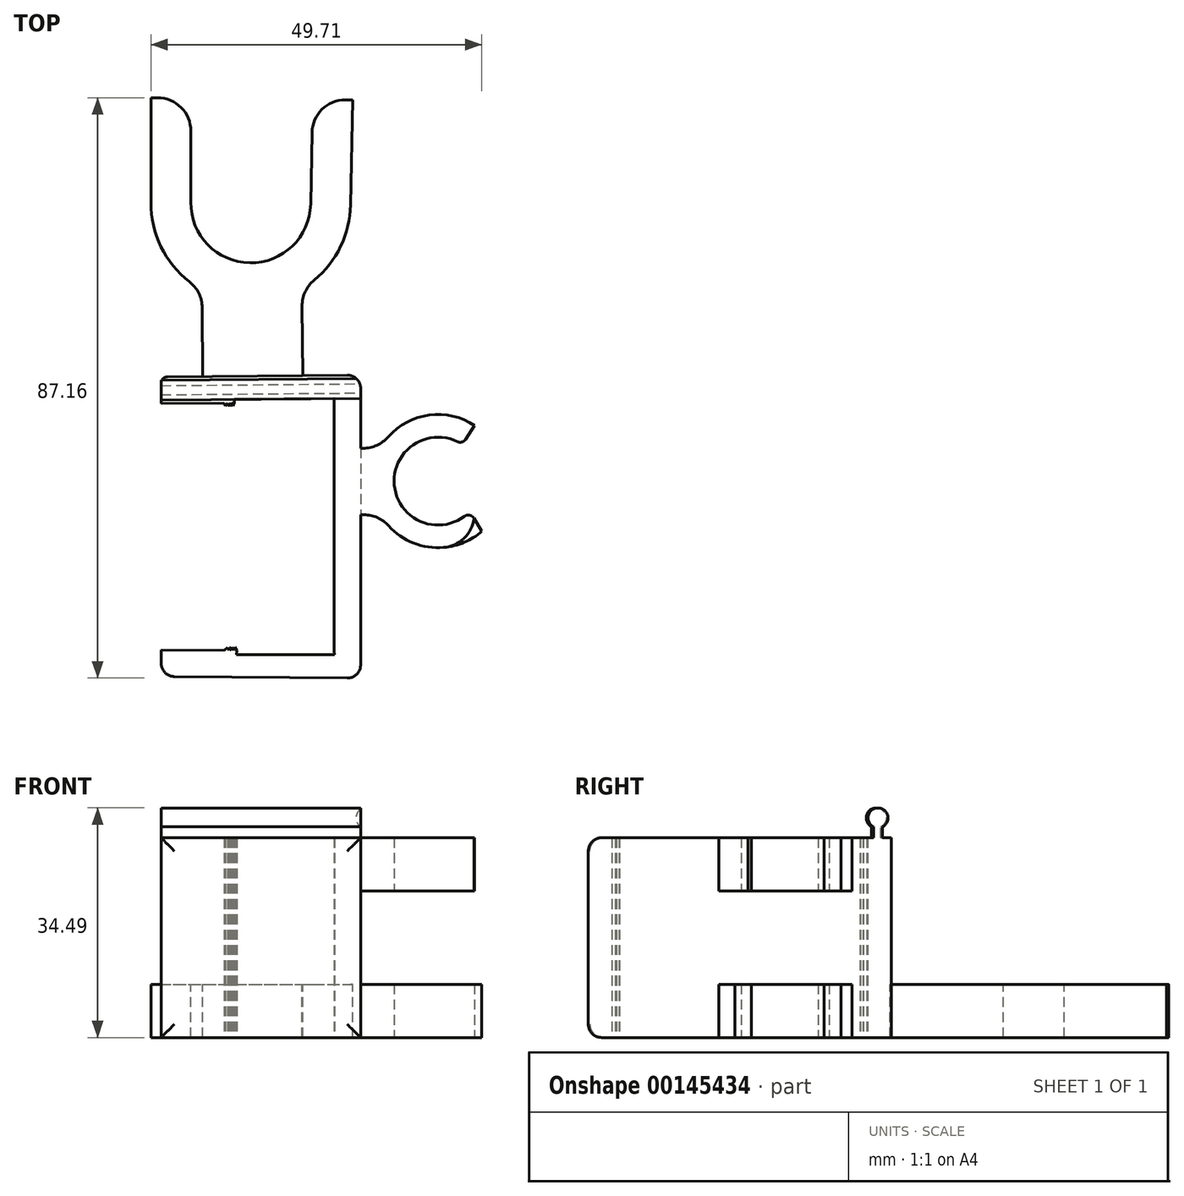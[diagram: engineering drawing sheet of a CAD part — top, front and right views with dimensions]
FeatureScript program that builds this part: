
annotation { "Feature Type Name" : "Feature", "Feature Type Description" : "" }
export const myFeature = defineFeature(function(context is Context, id is Id, definition is map)
    precondition{}
    {
        {
            var Q0;
            Q0=qCreatedBy(makeId("Top.planeOp"),FACE);
            var sketch = newSketch(context, id + "F0", { "sketchPlane" : qUnion([Q0])});
            skLineSegment(sketch, "E0", {"start": v(-19.4, 17.85) * mm, "end": v(-9.96, 17.94) * mm});
            skLineSegment(sketch, "E1", {"start": v(6.6, 18.08) * mm, "end": v(6.6, -19.37) * mm});
            skLineSegment(sketch, "E2", {"start": v(-19.4, 17.85) * mm, "end": v(-19.43, 21.85) * mm});
            skLineSegment(sketch, "E3", {"start": v(-19.43, 21.85) * mm, "end": v(10.57, 22.12) * mm});
            skLineSegment(sketch, "E4", {"start": v(10.57, 22.12) * mm, "end": v(10.57, -23.4) * mm});
            skLineSegment(sketch, "E5", {"start": v(-19.4, -19.15) * mm, "end": v(-19.4, -23.15) * mm});
            skLineSegment(sketch, "E6", {"start": v(-19.4, -23.15) * mm, "end": v(10.57, -23.4) * mm});
            skPoint(sketch, "E7", {"position": v(-8.4, 17.95) * mm});
            skLineSegment(sketch, "E8", {"start": v(6.6, -0.65) * mm, "end": v(-3.27, -0.73) * mm, "construction": true});
            skPoint(sketch, "E9.MirrorP", {"position": v(-8.06, -19.5) * mm});
            skLineSegment(sketch, "E10.MirrorCS", {"start": v(-8.6, 17.45) * mm, "end": v(-8.92, 17.94) * mm});
            skLineSegment(sketch, "E11.MirrorCS", {"start": v(-8.92, 17.94) * mm, "end": v(-9.18, 17.43) * mm});
            skLineSegment(sketch, "E12.MirrorCS", {"start": v(-9.75, 17.45) * mm, "end": v(-9.96, 17.94) * mm});
            skLineSegment(sketch, "E13.MirrorCS", {"start": v(-9.44, 17.94) * mm, "end": v(-9.75, 17.45) * mm});
            skLineSegment(sketch, "E14.MirrorCS", {"start": v(-9.18, 17.43) * mm, "end": v(-9.44, 17.94) * mm});
            skLineSegment(sketch, "E15.MirrorCS", {"start": v(-8.4, 17.95) * mm, "end": v(-8.6, 17.45) * mm});
            skPoint(sketch, "E16", {"position": v(-8.02, -19.25) * mm});
            skLineSegment(sketch, "E17", {"start": v(-8.02, -19.25) * mm, "end": v(-8.32, -18.74) * mm});
            skLineSegment(sketch, "E18", {"start": v(-8.32, -18.74) * mm, "end": v(-8.59, -19.24) * mm});
            skLineSegment(sketch, "E19", {"start": v(-8.59, -19.24) * mm, "end": v(-8.83, -18.75) * mm});
            skLineSegment(sketch, "E20", {"start": v(-8.83, -18.75) * mm, "end": v(-9.18, -19.24) * mm});
            skLineSegment(sketch, "E21", {"start": v(-9.18, -19.24) * mm, "end": v(-9.4, -18.76) * mm});
            skLineSegment(sketch, "E22", {"start": v(-9.4, -18.76) * mm, "end": v(-9.9, -19.23) * mm});
            skLineSegment(sketch, "E23.trimOffspring", {"start": v(-9.9, -19.23) * mm, "end": v(-19.4, -19.15) * mm});
            skLineSegment(sketch, "E24.bottom", {"start": v(10.57, 11.13) * mm, "end": v(13.49, 11.13) * mm});
            skLineSegment(sketch, "E24.top", {"start": v(10.57, 1.13) * mm, "end": v(13.56, 1.13) * mm});
            skLineSegment(sketch, "E24.left", {"start": v(10.57, 11.13) * mm, "end": v(10.57, 1.13) * mm});
            skArc(sketch, "E25", {"start": v(25.06, 12.13) * mm, "mid": v(15.61, 5.57) * mm, "end": v(26.12, 0.9) * mm});
            skArc(sketch, "E26", {"start": v(13.56, 1.13) * mm, "mid": v(20.58, -3.68) * mm, "end": v(28.76, -1.34) * mm});
            skPoint(sketch, "E27.orphan", {"position": v(22.18, 11.19) * mm});
            skPoint(sketch, "E28.orphan", {"position": v(22.18, 1.19) * mm});
            skLineSegment(sketch, "E29", {"start": v(26.33, 12.48) * mm, "end": v(27.69, 14.54) * mm});
            skLineSegment(sketch, "E30", {"start": v(27.58, 0.61) * mm, "end": v(28.76, -1.34) * mm});
            skArc(sketch, "E31.trimOffspring", {"start": v(27.69, 14.54) * mm, "mid": v(19.85, 15.91) * mm, "end": v(13.49, 11.13) * mm});
            skPoint(sketch, "E32.visualSharp", {"position": v(25.82, 11.7) * mm});
            skArc(sketch, "E32.filletArc", {"start": v(25.06, 12.13) * mm, "mid": v(25.76, 12.06) * mm, "end": v(26.33, 12.48) * mm});
            skPoint(sketch, "E33.visualSharp", {"position": v(26.96, 1.63) * mm});
            skArc(sketch, "E33.filletArc", {"start": v(27.58, 0.61) * mm, "mid": v(26.91, 1.07) * mm, "end": v(26.12, 0.9) * mm});
            skLineSegment(sketch, "E34", {"start": v(-8.4, 17.95) * mm, "end": v(-8.4, 18.45) * mm});
            skLineSegment(sketch, "E35", {"start": v(-8.4, 18.45) * mm, "end": v(6.6, 18.58) * mm});
            skLineSegment(sketch, "E36", {"start": v(6.6, 18.58) * mm, "end": v(6.6, 18.08) * mm});
            skLineSegment(sketch, "E37", {"start": v(-8.02, -19.25) * mm, "end": v(-8.06, -19.87) * mm});
            skLineSegment(sketch, "E38", {"start": v(-8.06, -19.87) * mm, "end": v(6.63, -19.87) * mm});
            skLineSegment(sketch, "E39", {"start": v(6.63, -19.87) * mm, "end": v(6.6, -19.37) * mm});
            skSolve(sketch);
        }
        {
            var Q0;
            Q0=makeQuery(id+"F0.imprint","IMPRINT",FACE,{"disambiguationData":[TD([[makeQuery(id+"F0.imprint","IMPRINT",EDGE,{"derivedFrom":sQuery(id+"F0.wireOp",EDGE,"E0")}),1.0]])]});
            extrude(context, id + "F1", {"entities" : qUnion([Q0]), "depth" : 30 * mm});
        }
        {
            var Q0;
            Q0=makeQuery(id+"F0.imprint","IMPRINT",FACE,{"disambiguationData":[TD([[makeQuery(id+"F0.imprint","IMPRINT",EDGE,{"derivedFrom":sQuery(id+"F0.wireOp",EDGE,"E24.bottom")}),-1.0]])]});
            extrude(context, id + "F2", {"entities" : qUnion([Q0]), "operationType" : NewBodyOperationType.ADD, "depth" : 8 * mm});
        }
        {
            var Q0;
            Q0=qCreatedBy(makeId("Top.planeOp"),FACE);
            cPlane(context, id + "F3", {"entities" : qUnion([Q0]), "cplaneType" : CPlaneType.OFFSET, "offset" : 22 * mm, "width" : 150 * mm, "height" : 150 * mm});
        }
        {
            var Q0;
            Q0=qCreatedBy(id+"F3.planeOp",FACE);
            var sketch = newSketch(context, id + "F4", { "sketchPlane" : qUnion([Q0])});
            skLineSegment(sketch, "E40.0", {"start": v(-19.4, 17.85) * mm, "end": v(-9.96, 17.94) * mm});
            skLineSegment(sketch, "E40.1", {"start": v(6.6, 18.08) * mm, "end": v(6.6, -19.37) * mm});
            skLineSegment(sketch, "E40.2", {"start": v(6.6, -19.37) * mm, "end": v(-8.02, -19.25) * mm});
            skLineSegment(sketch, "E40.3", {"start": v(-19.4, 17.85) * mm, "end": v(-19.43, 21.85) * mm});
            skLineSegment(sketch, "E40.4", {"start": v(-19.43, 21.85) * mm, "end": v(10.57, 22.12) * mm});
            skLineSegment(sketch, "E40.5", {"start": v(10.57, 22.12) * mm, "end": v(10.57, -23.4) * mm});
            skLineSegment(sketch, "E40.6", {"start": v(-19.4, -19.15) * mm, "end": v(-19.4, -23.15) * mm});
            skLineSegment(sketch, "E40.7", {"start": v(-19.4, -23.15) * mm, "end": v(10.57, -23.4) * mm});
            skPoint(sketch, "E40.8", {"position": v(-8.4, 17.95) * mm});
            skLineSegment(sketch, "E40.9", {"start": v(6.6, -0.65) * mm, "end": v(-3.27, -0.73) * mm});
            skPoint(sketch, "E40.10", {"position": v(-8.06, -19.5) * mm});
            skLineSegment(sketch, "E40.11", {"start": v(-8.6, 17.45) * mm, "end": v(-8.92, 17.94) * mm});
            skLineSegment(sketch, "E40.12", {"start": v(-8.92, 17.94) * mm, "end": v(-9.18, 17.43) * mm});
            skPoint(sketch, "E40.13", {"position": v(-8.4, 17.95) * mm});
            skLineSegment(sketch, "E40.14", {"start": v(-9.75, 17.45) * mm, "end": v(-9.96, 17.94) * mm});
            skLineSegment(sketch, "E40.15", {"start": v(-9.44, 17.94) * mm, "end": v(-9.75, 17.45) * mm});
            skLineSegment(sketch, "E40.16", {"start": v(-9.18, 17.43) * mm, "end": v(-9.44, 17.94) * mm});
            skLineSegment(sketch, "E40.17", {"start": v(-8.4, 17.95) * mm, "end": v(-8.6, 17.45) * mm});
            skPoint(sketch, "E40.18", {"position": v(-8.02, -19.25) * mm});
            skLineSegment(sketch, "E40.19", {"start": v(-8.02, -19.25) * mm, "end": v(-8.32, -18.74) * mm});
            skLineSegment(sketch, "E40.20", {"start": v(-8.32, -18.74) * mm, "end": v(-8.59, -19.24) * mm});
            skLineSegment(sketch, "E40.21", {"start": v(-8.59, -19.24) * mm, "end": v(-8.83, -18.75) * mm});
            skLineSegment(sketch, "E40.22", {"start": v(-8.83, -18.75) * mm, "end": v(-9.18, -19.24) * mm});
            skLineSegment(sketch, "E40.23", {"start": v(-9.18, -19.24) * mm, "end": v(-9.4, -18.76) * mm});
            skLineSegment(sketch, "E40.24", {"start": v(-9.4, -18.76) * mm, "end": v(-9.9, -19.23) * mm});
            skLineSegment(sketch, "E40.25", {"start": v(-9.9, -19.23) * mm, "end": v(-19.4, -19.15) * mm});
            skLineSegment(sketch, "E40.26", {"start": v(-8.4, 18.95) * mm, "end": v(6.6, 19.08) * mm});
            skLineSegment(sketch, "E40.27", {"start": v(10.57, 11.13) * mm, "end": v(13.49, 11.13) * mm});
            skLineSegment(sketch, "E40.28", {"start": v(10.57, 1.13) * mm, "end": v(13.56, 1.13) * mm});
            skLineSegment(sketch, "E40.29", {"start": v(10.57, 11.13) * mm, "end": v(10.57, 1.13) * mm});
            skArc(sketch, "E40.30", {"start": v(25.06, 12.13) * mm, "mid": v(15.61, 5.57) * mm, "end": v(26.12, 0.9) * mm});
            skArc(sketch, "E40.31", {"start": v(13.56, 1.13) * mm, "mid": v(20.58, -3.68) * mm, "end": v(28.76, -1.34) * mm});
            skPoint(sketch, "E40.32", {"position": v(22.18, 11.19) * mm});
            skPoint(sketch, "E40.33", {"position": v(22.18, 1.19) * mm});
            skLineSegment(sketch, "E40.34", {"start": v(26.33, 12.48) * mm, "end": v(27.69, 14.54) * mm});
            skLineSegment(sketch, "E40.35", {"start": v(27.58, 0.61) * mm, "end": v(28.76, -1.34) * mm});
            skArc(sketch, "E40.36", {"start": v(27.69, 14.54) * mm, "mid": v(19.85, 15.91) * mm, "end": v(13.49, 11.13) * mm});
            skPoint(sketch, "E40.37", {"position": v(25.82, 11.7) * mm});
            skArc(sketch, "E40.38", {"start": v(25.06, 12.13) * mm, "mid": v(25.76, 12.06) * mm, "end": v(26.33, 12.48) * mm});
            skPoint(sketch, "E40.39", {"position": v(26.96, 1.63) * mm});
            skArc(sketch, "E40.40", {"start": v(27.58, 0.61) * mm, "mid": v(26.91, 1.07) * mm, "end": v(26.12, 0.9) * mm});
            skLineSegment(sketch, "E40.42", {"start": v(10.57, 1.13) * mm, "end": v(13.56, 1.13) * mm});
            skSolve(sketch);
        }
        {
            var Q0;
            Q0=makeQuery(id+"F4.imprint","IMPRINT",FACE,{"disambiguationData":[TD([[makeQuery(id+"F4.imprint","IMPRINT",EDGE,{"derivedFrom":sQuery(id+"F4.wireOp",EDGE,"E40.27")}),-1.0]])]});
            var Q1;
            Q1=makeQuery(id+"F1.opExtrude","CAP_FACE",FACE,{"disambiguationData":[OSD([sQuery(id+"F0.wireOp",EDGE,"E0"),sQuery(id+"F0.wireOp",EDGE,"E1"),sQuery(id+"F0.wireOp",EDGE,"WWZshYS6-7xGF-DUjU-nE3Z-Lly4ewc0VkBt"),sQuery(id+"F0.wireOp",EDGE,"E2"),sQuery(id+"F0.wireOp",EDGE,"E3"),sQuery(id+"F0.wireOp",EDGE,"E4"),sQuery(id+"F0.wireOp",EDGE,"E5"),sQuery(id+"F0.wireOp",EDGE,"E6"),sQuery(id+"F0.wireOp",EDGE,"E10.MirrorCS"),sQuery(id+"F0.wireOp",EDGE,"E11.MirrorCS"),sQuery(id+"F0.wireOp",EDGE,"E12.MirrorCS"),sQuery(id+"F0.wireOp",EDGE,"E13.MirrorCS"),sQuery(id+"F0.wireOp",EDGE,"E14.MirrorCS"),sQuery(id+"F0.wireOp",EDGE,"E15.MirrorCS"),sQuery(id+"F0.wireOp",EDGE,"E17"),sQuery(id+"F0.wireOp",EDGE,"E18"),sQuery(id+"F0.wireOp",EDGE,"E19"),sQuery(id+"F0.wireOp",EDGE,"E20"),sQuery(id+"F0.wireOp",EDGE,"E21"),sQuery(id+"F0.wireOp",EDGE,"E22"),sQuery(id+"F0.wireOp",EDGE,"E23.trimOffspring"),sQuery(id+"F0.wireOp",EDGE,"4b8f868b-2b8d-4027-893b-67bc05272e9b.trimOffspring"),sQuery(id+"F0.wireOp",EDGE,"E24.left")])],"isStart":false});
            extrude(context, id + "F5", {"entities" : qUnion([Q0]), "operationType" : NewBodyOperationType.ADD, "endBound" : BoundingType.UP_TO_SURFACE, "endBoundEntityFace" : qUnion([Q1]), "depth" : 25 * mm});
        }
        {
            var Q0;
            Q0=makeQuery(id+"F1.opExtrude","SWEPT_FACE",FACE,{"disambiguationData":[OSD([sQuery(id+"F0.wireOp",EDGE,"E3")])]});
            var sketch = newSketch(context, id + "F6", { "sketchPlane" : qUnion([Q0])});
            skLineSegment(sketch, "E41.bottom", {"start": v(12.95, 0) * mm, "end": v(-2.05, 0) * mm});
            skLineSegment(sketch, "E41.top", {"start": v(12.95, 8) * mm, "end": v(-2.05, 8) * mm});
            skLineSegment(sketch, "E41.left", {"start": v(12.95, 0) * mm, "end": v(12.95, 8) * mm});
            skLineSegment(sketch, "E41.right", {"start": v(-2.05, 0) * mm, "end": v(-2.05, 8) * mm});
            skSolve(sketch);
        }
        {
            var Q0;
            Q0 = qSketchRegion(id + "F6", true);
            extrude(context, id + "F7", {"entities" : qUnion([Q0]), "operationType" : NewBodyOperationType.ADD, "depth" : 17 * mm});
        }
        {
            var Q0;
            Q0=qCreatedBy(makeId("Top.planeOp"),FACE);
            cPlane(context, id + "F8", {"entities" : qUnion([Q0]), "cplaneType" : CPlaneType.OFFSET, "offset" : 8 * mm, "width" : 150 * mm, "height" : 150 * mm});
        }
        {
            var Q0;
            Q0=qCreatedBy(id+"F8.planeOp",FACE);
            var sketch = newSketch(context, id + "F9", { "sketchPlane" : qUnion([Q0])});
            skLineSegment(sketch, "E42.0", {"start": v(-13.3, 38.9) * mm, "end": v(1.7, 39.04) * mm});
            skArc(sketch, "E43", {"start": v(-14.95, 48.08) * mm, "mid": v(-6.09, 38.97) * mm, "end": v(3.05, 47.8) * mm});
            skArc(sketch, "E44", {"start": v(-20.95, 48.02) * mm, "mid": v(-6.12, 32.97) * mm, "end": v(9.05, 47.68) * mm});
            skLineSegment(sketch, "E45", {"start": v(-14.95, 48.08) * mm, "end": v(-14.95, 63.77) * mm});
            skLineSegment(sketch, "E46", {"start": v(-14.95, 63.77) * mm, "end": v(-20.95, 63.77) * mm});
            skLineSegment(sketch, "E47", {"start": v(-20.95, 63.77) * mm, "end": v(-20.95, 48.02) * mm});
            skLineSegment(sketch, "E48", {"start": v(3.05, 47.8) * mm, "end": v(3.36, 63.45) * mm});
            skLineSegment(sketch, "E49", {"start": v(3.36, 63.45) * mm, "end": v(9.36, 63.45) * mm});
            skLineSegment(sketch, "E50", {"start": v(9.36, 63.45) * mm, "end": v(9.05, 47.68) * mm});
            skSolve(sketch);
        }
        {
            var Q0;
            Q0=makeQuery(id+"F9.imprint","IMPRINT",FACE,{"disambiguationData":[TD([[makeQuery(id+"F9.imprint","IMPRINT",EDGE,{"derivedFrom":sQuery(id+"F9.wireOp",EDGE,"E44")}),1.0]])]});
            var Q1;
            {var subQ0=sQuery(id+"F0.wireOp",EDGE,"E24.left");Q1=makeQuery(id+"F7.boolean.opBoolean","MERGE",FACE,{"derivedFrom":[makeQuery(id+"F2.boolean.opBoolean","MERGE",FACE,{"derivedFrom":[makeQuery(id+"F1.opExtrude","CAP_FACE",FACE,{"disambiguationData":[OSD([sQuery(id+"F0.wireOp",EDGE,"E0"),sQuery(id+"F0.wireOp",EDGE,"E1"),sQuery(id+"F0.wireOp",EDGE,"WWZshYS6-7xGF-DUjU-nE3Z-Lly4ewc0VkBt"),sQuery(id+"F0.wireOp",EDGE,"E2"),sQuery(id+"F0.wireOp",EDGE,"E3"),sQuery(id+"F0.wireOp",EDGE,"E4"),sQuery(id+"F0.wireOp",EDGE,"E5"),sQuery(id+"F0.wireOp",EDGE,"E6"),sQuery(id+"F0.wireOp",EDGE,"E10.MirrorCS"),sQuery(id+"F0.wireOp",EDGE,"E11.MirrorCS"),sQuery(id+"F0.wireOp",EDGE,"E12.MirrorCS"),sQuery(id+"F0.wireOp",EDGE,"E13.MirrorCS"),sQuery(id+"F0.wireOp",EDGE,"E14.MirrorCS"),sQuery(id+"F0.wireOp",EDGE,"E15.MirrorCS"),sQuery(id+"F0.wireOp",EDGE,"E17"),sQuery(id+"F0.wireOp",EDGE,"E18"),sQuery(id+"F0.wireOp",EDGE,"E19"),sQuery(id+"F0.wireOp",EDGE,"E20"),sQuery(id+"F0.wireOp",EDGE,"E21"),sQuery(id+"F0.wireOp",EDGE,"E22"),sQuery(id+"F0.wireOp",EDGE,"E23.trimOffspring"),sQuery(id+"F0.wireOp",EDGE,"4b8f868b-2b8d-4027-893b-67bc05272e9b.trimOffspring"),subQ0])],"isStart":true}),makeQuery(id+"F2.opExtrude","CAP_FACE",FACE,{"disambiguationData":[OSD([sQuery(id+"F0.wireOp",EDGE,"E24.bottom"),sQuery(id+"F0.wireOp",EDGE,"E24.top"),subQ0,sQuery(id+"F0.wireOp",EDGE,"E25"),sQuery(id+"F0.wireOp",EDGE,"E26"),sQuery(id+"F0.wireOp",EDGE,"E29"),sQuery(id+"F0.wireOp",EDGE,"E30"),sQuery(id+"F0.wireOp",EDGE,"E31.trimOffspring"),sQuery(id+"F0.wireOp",EDGE,"E32.filletArc"),sQuery(id+"F0.wireOp",EDGE,"E33.filletArc"),sQuery(id+"F0.wireOp",EDGE,"JSLU7fQd-V2J5-IQyR-vvuS-VnIauMRNyzz8")])],"isStart":true})]}),makeQuery(id+"F7.opExtrude","SWEPT_FACE",FACE,{"disambiguationData":[OSD([sQuery(id+"F6.wireOp",EDGE,"E41.bottom")])]})]});}
            extrude(context, id + "F10", {"entities" : qUnion([Q0]), "operationType" : NewBodyOperationType.ADD, "endBound" : BoundingType.UP_TO_SURFACE, "oppositeDirection" : true, "endBoundEntityFace" : qUnion([Q1]), "depth" : 25 * mm});
        }
        {
            var Q0;
            Q0=makeQuery(id+"F1.opExtrude","SWEPT_FACE",FACE,{"disambiguationData":[OSD([sQuery(id+"F0.wireOp",EDGE,"E2")])]});
            var sketch = newSketch(context, id + "F11", { "sketchPlane" : qUnion([Q0])});
            skLineSegment(sketch, "E51.bottom", {"start": v(-19.33, 29.99) * mm, "end": v(-19.33, 31.66) * mm});
            skLineSegment(sketch, "E51.top", {"start": v(-20.71, 29.99) * mm, "end": v(-20.71, 31.66) * mm});
            skLineSegment(sketch, "E51.left", {"start": v(-19.33, 29.99) * mm, "end": v(-20.71, 29.99) * mm});
            skArc(sketch, "E52", {"start": v(-19.33, 31.66) * mm, "mid": v(-20.02, 34.49) * mm, "end": v(-20.71, 31.66) * mm});
            skPoint(sketch, "E53.orphan", {"position": v(-19.33, 32.94) * mm});
            skPoint(sketch, "E54.orphan", {"position": v(-20.71, 33.04) * mm});
            skPoint(sketch, "E55", {"position": v(-20.02, 29.99) * mm});
            skPoint(sketch, "E55.positionSnap0", {"position": v(-20.02, 30) * mm});
            skSolve(sketch);
        }
        {
            var Q0;
            Q0=makeQuery(id+"F11.imprint","IMPRINT",FACE,{"disambiguationData":[TD([[makeQuery(id+"F11.imprint","IMPRINT",EDGE,{"derivedFrom":sQuery(id+"F11.wireOp",EDGE,"E51.bottom")}),1.0]])]});
            var Q1;
            Q1=makeQuery(id+"F1.opExtrude","SWEPT_FACE",FACE,{"disambiguationData":[OSD([sQuery(id+"F0.wireOp",EDGE,"E4"),sQuery(id+"F0.wireOp",EDGE,"E24.left")])]});
            extrude(context, id + "F12", {"entities" : qUnion([Q0]), "operationType" : NewBodyOperationType.ADD, "endBound" : BoundingType.UP_TO_SURFACE, "oppositeDirection" : true, "endBoundEntityFace" : qUnion([Q1]), "depth" : 25 * mm});
        }
        {
            var Q0;
            Q0=makeQuery(id+"F7.opExtrude","CAP_EDGE",EDGE,{"disambiguationData":[OSD([sQuery(id+"F6.wireOp",EDGE,"E41.left")])],"isStart":true});
            var Q1;
            Q1=makeQuery(id+"F7.opExtrude","CAP_EDGE",EDGE,{"disambiguationData":[OSD([sQuery(id+"F6.wireOp",EDGE,"E41.right")])],"isStart":true});
            var Q2;
            Q2=makeQuery(id+"F2.opExtrude","SWEPT_EDGE",EDGE,{"disambiguationData":[OSD([sQuery(id+"F0.wireOp",EDGE,"E4"),sQuery(id+"F0.wireOp",EDGE,"E24.bottom"),sQuery(id+"F0.wireOp",EDGE,"E24.left")])]});
            var Q3;
            Q3=makeQuery(id+"F5.opExtrude","SWEPT_EDGE",EDGE,{"disambiguationData":[OSD([sQuery(id+"F4.wireOp",EDGE,"E40.5"),sQuery(id+"F4.wireOp",EDGE,"E40.27"),sQuery(id+"F4.wireOp",EDGE,"E40.29")])]});
            var Q4;
            Q4=makeQuery(id+"F2.opExtrude","SWEPT_EDGE",EDGE,{"disambiguationData":[OSD([sQuery(id+"F0.wireOp",EDGE,"E4"),sQuery(id+"F0.wireOp",EDGE,"E24.top"),sQuery(id+"F0.wireOp",EDGE,"E24.left")])]});
            var Q5;
            Q5=makeQuery(id+"F5.opExtrude","SWEPT_EDGE",EDGE,{"disambiguationData":[OSD([sQuery(id+"F4.wireOp",EDGE,"E40.5"),sQuery(id+"F4.wireOp",EDGE,"E40.29"),sQuery(id+"F4.wireOp",EDGE,"E40.42")])]});
            var Q6;
            Q6=makeQuery(id+"F2.opExtrude","SWEPT_EDGE",EDGE,{"disambiguationData":[OSD([sQuery(id+"F0.wireOp",EDGE,"E24.top"),sQuery(id+"F0.wireOp",EDGE,"E26")])]});
            var Q7;
            Q7=makeQuery(id+"F2.opExtrude","SWEPT_EDGE",EDGE,{"disambiguationData":[OSD([sQuery(id+"F0.wireOp",EDGE,"E24.bottom"),sQuery(id+"F0.wireOp",EDGE,"E31.trimOffspring")])]});
            var Q8;
            Q8=makeQuery(id+"F5.opExtrude","SWEPT_EDGE",EDGE,{"disambiguationData":[OSD([sQuery(id+"F4.wireOp",EDGE,"E40.27"),sQuery(id+"F4.wireOp",EDGE,"E40.36")])]});
            var Q9;
            Q9=makeQuery(id+"F5.opExtrude","SWEPT_EDGE",EDGE,{"disambiguationData":[OSD([sQuery(id+"F4.wireOp",EDGE,"E40.31"),sQuery(id+"F4.wireOp",EDGE,"E40.42")])]});
            var Q10;
            Q10=makeQuery(id+"F10.boolean.opBoolean","INTERSECT",EDGE,{"derivedFrom":[makeQuery(id+"F7.opExtrude","SWEPT_FACE",FACE,{"disambiguationData":[OSD([sQuery(id+"F6.wireOp",EDGE,"E41.right")])]}),makeQuery(id+"F10.opExtrude","SWEPT_FACE",FACE,{"disambiguationData":[OSD([sQuery(id+"F9.wireOp",EDGE,"E44")])]})]});
            var Q11;
            Q11=makeQuery(id+"F10.boolean.opBoolean","INTERSECT",EDGE,{"derivedFrom":[makeQuery(id+"F7.opExtrude","SWEPT_FACE",FACE,{"disambiguationData":[OSD([sQuery(id+"F6.wireOp",EDGE,"E41.left")])]}),makeQuery(id+"F10.opExtrude","SWEPT_FACE",FACE,{"disambiguationData":[OSD([sQuery(id+"F9.wireOp",EDGE,"E44")])]})]});
            var Q12;
            Q12=makeQuery(id+"F10.opExtrude","SWEPT_EDGE",EDGE,{"disambiguationData":[OSD([sQuery(id+"F9.wireOp",EDGE,"E45"),sQuery(id+"F9.wireOp",EDGE,"E46")])]});
            var Q13;
            Q13=makeQuery(id+"F10.opExtrude","SWEPT_EDGE",EDGE,{"disambiguationData":[OSD([sQuery(id+"F9.wireOp",EDGE,"E48"),sQuery(id+"F9.wireOp",EDGE,"E49")])]});
            fillet(context, id + "F13", {"entities" : qUnion([Q0, Q1, Q2, Q3, Q4, Q5, Q6, Q7, Q8, Q9, Q10, Q11, Q12, Q13]), "radius" : 5 * mm, "tangentPropagation" : true, "allowEdgeOverflow" : false});
        }
        {
            var Q0;
            Q0=makeQuery(id+"F1.opExtrude","SWEPT_EDGE",EDGE,{"disambiguationData":[OSD([sQuery(id+"F0.wireOp",EDGE,"E4"),sQuery(id+"F0.wireOp",EDGE,"E6")])]});
            var Q1;
            Q1=makeQuery(id+"F1.opExtrude","CAP_EDGE",EDGE,{"disambiguationData":[OSD([sQuery(id+"F0.wireOp",EDGE,"E6")])],"isStart":false});
            var Q2;
            Q2=makeQuery(id+"F1.opExtrude","SWEPT_EDGE",EDGE,{"disambiguationData":[OSD([sQuery(id+"F0.wireOp",EDGE,"E5"),sQuery(id+"F0.wireOp",EDGE,"E6")])]});
            var Q3;
            Q3=makeQuery(id+"F1.opExtrude","CAP_EDGE",EDGE,{"disambiguationData":[OSD([sQuery(id+"F0.wireOp",EDGE,"E6")])],"isStart":true});
            var Q4;
            {var subQ11=sQuery(id+"F0.wireOp",EDGE,"E4");var subQ12=sQuery(id+"F0.wireOp",EDGE,"E3");var subQ33=sQuery(id+"F6.wireOp",EDGE,"E41.bottom");Q4=makeQuery(id+"F12.boolean.opBoolean","SPLIT",EDGE,{"disambiguationData":[TD([makeQuery(id+"F7.opExtrude","SWEPT_FACE",FACE,{"disambiguationData":[OSD([subQ33])]})])],"derivedFrom":makeQuery(id+"F1.opExtrude","SWEPT_EDGE",EDGE,{"disambiguationData":[OSD([subQ12,subQ11])]})});}
            fillet(context, id + "F14", {"entities" : qUnion([Q0, Q1, Q2, Q3, Q4]), "radius" : 2 * mm, "tangentPropagation" : true, "allowEdgeOverflow" : false});
        }
        {
            var Q0;
            {var subQ0=sQuery(id+"F0.wireOp",EDGE,"E3");var subQ12=sQuery(id+"F0.wireOp",EDGE,"E2");var subQ34=sQuery(id+"F6.wireOp",EDGE,"E41.bottom");Q0=makeQuery(id+"F12.boolean.opBoolean","SPLIT",EDGE,{"disambiguationData":[TD([makeQuery(id+"F7.opExtrude","SWEPT_FACE",FACE,{"disambiguationData":[OSD([subQ34])]})])],"derivedFrom":makeQuery(id+"F1.opExtrude","SWEPT_EDGE",EDGE,{"disambiguationData":[OSD([subQ12,subQ0])]})});}
            fillet(context, id + "F15", {"entities" : qUnion([Q0]), "radius" : 1 * mm, "tangentPropagation" : true, "allowEdgeOverflow" : false});
        }
    });
